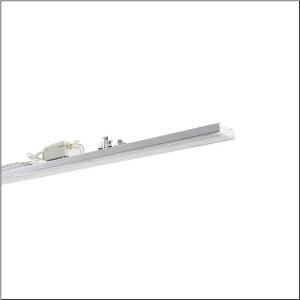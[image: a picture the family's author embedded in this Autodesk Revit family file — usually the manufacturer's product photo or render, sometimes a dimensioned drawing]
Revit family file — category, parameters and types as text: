
# Revit family: licross_11_recessed_mo_51te12dv4fxg
name_source: partatom
category: Lighting Fixtures
units: mm (PartAtom-declared; Revit-internal decimal feet)

## family parameters
Cut with Voids When Loaded = No
Host = Face
Light Source = No
Part Type = Normal
Room Calculation Point = No
Round Connector Dimension = Use Diameter
Shared = No

## types (1)
- --- (1 x LED, 15360 lm, 84.1 W, 4000K)
    Apparent Load = 84 VA
    CIE Flux Codes = 67 92 99 100 100
    Color Rendering = 80
    Color Temperature = 4000K
    Default Elevation = 1800 mm
    Description = Licross 11 Recessed MO, luminaire insert, of sheet steel, galvanised, coil coated, white, length: 2.250mm, width: 66mm, height: 67mm, LED rated luminous flux: 15.360lm, light colour: 840, SDCM (Standard Deviation of Colour Matching)MacAdam ≤ 2 SDCM (initial), control gear: DALI 2, with plug, 5-pole, with phase selection, mains connection: 220..240V, AC, 50/60Hz, rated input power: 84W, internal wiring halogen-free, primary optical cover: cover, of PMMA, light emission: direct distribution, primary light characteristic: symmetric, protection rating (complete): IP54, insulation class (complete): insulation class I (protective earthing), certification: CE, ENEC, VDE, UKCA, protection symbol: D if used in an environment with non-conductive dust loads with corresponding accessories, impact resistance: IK06, permissible ambient temperature for indoor applications: -25..+35°C, corresponds to IFS (International Featured Standards) requirements for safety and quality in the food industry, reducing of maximum allowable ambient temperature of 5°C with ceiling mounting, LABS conformity tested according to VDMA 24364:2018-05, The light source and the operating device comply with the requirements of the Ecodesign Regulation (EU) 2019/2020 and are replaceable in accordance with this regulation, packaging unit: 1 piece
    Height = 58 mm
    Lamp = 1 x LED
    Lamp Light Flux = 15360 lm
    Lamp Power = 84.1 W
    Lamp count = 1
    Length = 2250 mm
    Luminous efficacy = 183 lm/W
    Manufacturer = Siteco
    ModVariant = No
    Model = 51TE12DV4FXG
    Mounting Place = Ceiling
    Mounting Type = Pendant
    Number of Poles = 1
    OnlyDefault = Yes
    Power Factor = 1
    Product Name = Licross 11 Recessed MO
    Product group = luminaire insert | ceiling pendant
    ProductGroupID = 901
    Protection Class = Protection class I
    Protection Degree = IP 54
    RLX_Detail_Level = 1
    RLX_Emergency_Light_Flux = 0 lm
    RLX_Emergency_Type = 0
    RLX_Emergency_Type_DB = No
    RlxData = <blob elided: 29669 chars, md5=f0d72a72>
    Socket = socket
    Standby Power = 0 W
    System Light Flux = 15360 lm
    System Power = 84 W
    Type Comments = factory setting: luminous flux: 100 % | dim-lin: 254 | 378 mA
    Type Image = l_1296930.jpg
    URL = http://relux.com
    VarID = @adj_103285
    Voltage = 0 V
    Weight = 0.00 kg
    Width = 66 mm

## geometry (parser evidence)
native form markers: Blend x4, Sweep x10
no freeform markers — native parametric forms only
